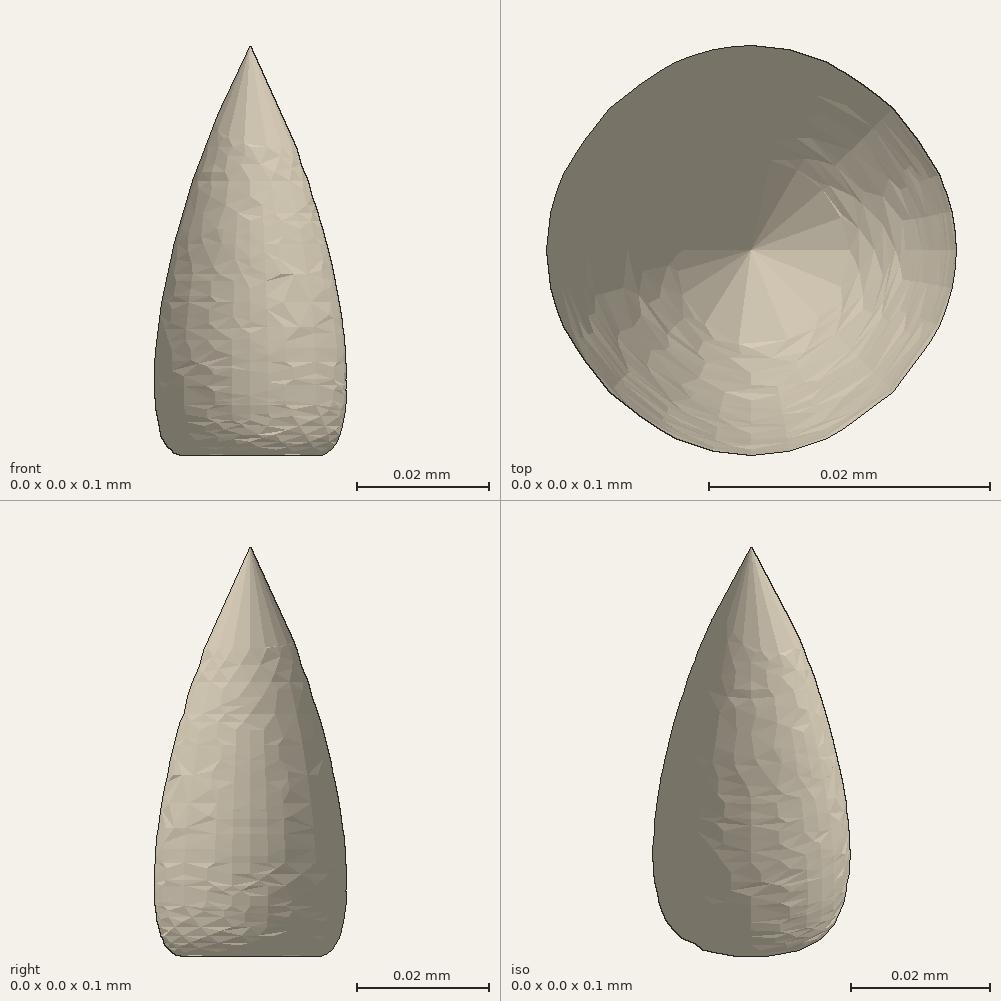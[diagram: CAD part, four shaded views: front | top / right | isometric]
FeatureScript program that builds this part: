
annotation { "Feature Type Name" : "Feature", "Feature Type Description" : "" }
export const myFeature = defineFeature(function(context is Context, id is Id, definition is map)
    precondition{}
    {
        {
            var Q0;
            Q0=qCreatedBy(makeId("Front.planeOp"),FACE);
            var sketch = newSketch(context, id + "F0", { "sketchPlane" : qUnion([Q0])});
            skFitSpline(sketch, "E0", {"points": [v(0, 0) * mm, v(16.97, 0) * mm, v(7.46, 5.44) * mm, v(6.9, 13.1) * mm, v(10.8, 18.93) * mm, v(19.9, 23.6) * mm, v(24.88, 28.84) * mm, v(25.1, 36.4) * mm, v(23.52, 40.55) * mm, v(23.01, 40.29) * mm, v(23.86, 37.18) * mm, v(24.3, 30.11) * mm, v(19.85, 24.83) * mm, v(11.71, 21.36) * mm, v(0, 19.73) * mm, v(0, 19.68) * mm], "startDerivative": vector(236.15, 8.5) * mm, "endDerivative": vector(8.76, 18.68) * mm});
            skLineSegment(sketch, "E1", {"start": v(0, 34) * mm, "end": v(0, -12.16) * mm});
            skSolve(sketch);
        }
        {
            var Q0;
            {var subQ0=sQuery(id+"F0.wireOp",EDGE,"E1");var subQ1=sQuery(id+"F0.wireOp",EDGE,"E0");var subQ2=makeQuery(id+"F0.imprint","INTERSECT",VERTEX,{"disambiguationData":[OD(0.0)],"derivedFrom":[subQ1,subQ0]});Q0=makeQuery(id+"F0.imprint","IMPRINT",FACE,{"disambiguationData":[TD([[makeQuery(id+"F0.imprint","IMPRINT",EDGE,{"disambiguationData":[TD([[subQ2,-1.0]])],"derivedFrom":subQ1}),1.0]])]});}
            var Q1;
            Q1=sQuery(id+"F0.wireOp",EDGE,"E1");
            revolve(context, id + "F1", {"surfaceOperationType" : NewSurfaceOperationType.NEW, "entities" : qUnion([Q0]), "axis" : qUnion([Q1]), "revolveType" : RevolveType.FULL});
        }
    });
